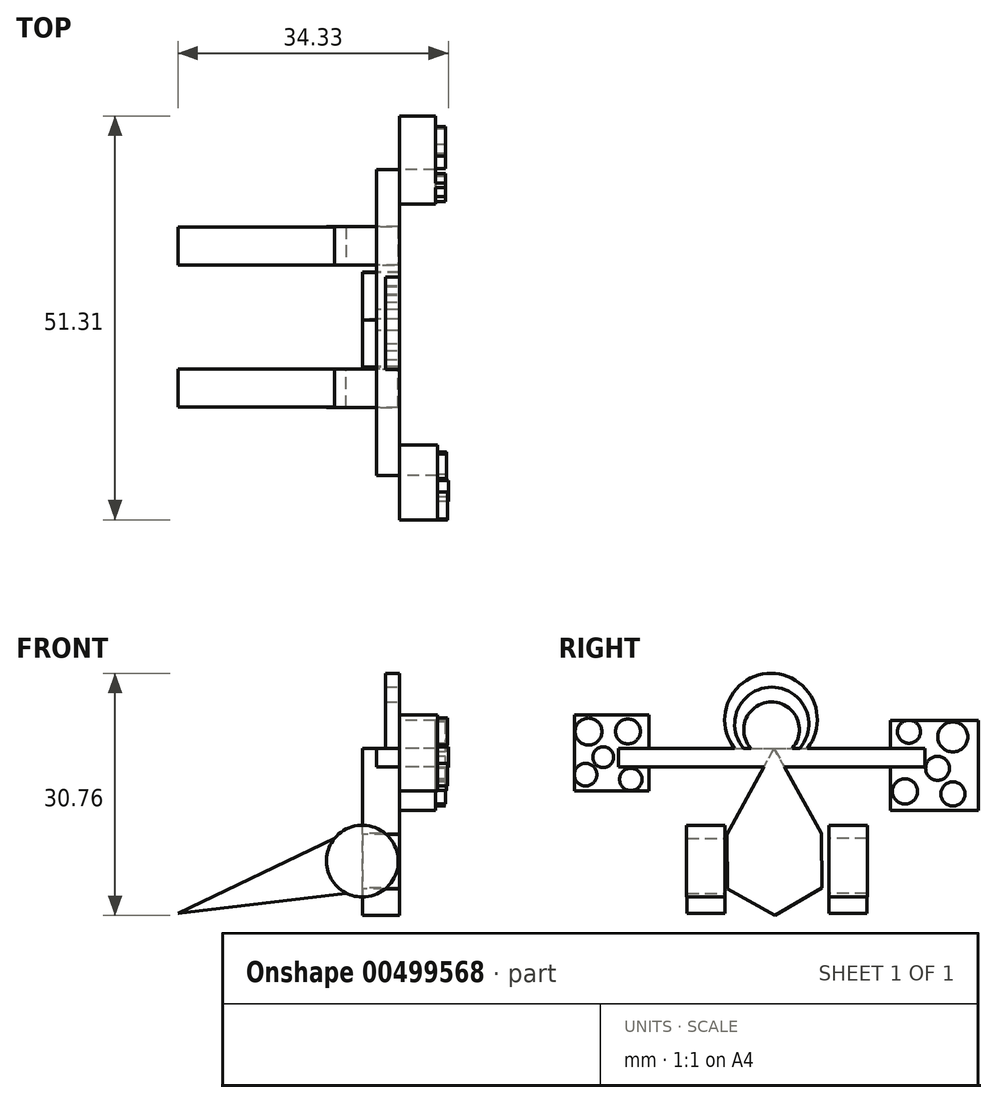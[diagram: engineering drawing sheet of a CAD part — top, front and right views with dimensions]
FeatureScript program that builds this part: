
annotation { "Feature Type Name" : "Feature", "Feature Type Description" : "" }
export const myFeature = defineFeature(function(context is Context, id is Id, definition is map)
    precondition{}
    {
        {
            var Q0;
            Q0=qCreatedBy(makeId("Front.planeOp"),FACE);
            var sketch = newSketch(context, id + "F0", { "sketchPlane" : qUnion([Q0])});
            skCircle(sketch, "E0", {"center": v(0, 0) * mm, "radius": 91.11 * mm});
            skSolve(sketch);
        }
        {
            var Q0;
            Q0=makeQuery(id+"F0.imprint","IMPRINT",FACE,{"disambiguationData":[TD([[makeQuery(id+"F0.imprint","IMPRINT",EDGE,{"derivedFrom":sQuery(id+"F0.wireOp",EDGE,"E0")}),1.0]])]});
            extrude(context, id + "F1", {"entities" : qUnion([Q0]), "depth" : 98.04 * mm});
        }
        {
            var Q0;
            Q0=makeQuery(id+"F1.opExtrude","CAP_FACE",FACE,{"disambiguationData":[OSD([sQuery(id+"F0.wireOp",EDGE,"E0")])],"isStart":true});
            var sketch = newSketch(context, id + "F2", { "sketchPlane" : qUnion([Q0])});
            skLineSegment(sketch, "E1", {"start": v(0, 91.11) * mm, "end": v(-434.23, -92.92) * mm});
            skLineSegment(sketch, "E2", {"start": v(0, -76.65) * mm, "end": v(-434.23, -92.92) * mm});
            skLineSegment(sketch, "E3", {"start": v(0, 91.11) * mm, "end": v(468.1, -132.24) * mm});
            skLineSegment(sketch, "E4", {"start": v(468.1, -132.24) * mm, "end": v(0, -76.65) * mm});
            skSolve(sketch);
        }
        {
            var Q0;
            {var subQ0=sQuery(id+"F2.wireOp",EDGE,"E4");var subQ1=sQuery(id+"F2.wireOp",EDGE,"E3");var subQ2=makeQuery(id+"F2.imprint","INTERSECT",VERTEX,{"derivedFrom":[subQ1,subQ0]});Q0=makeQuery(id+"F2.imprint","IMPRINT",FACE,{"disambiguationData":[TD([[makeQuery(id+"F2.imprint","IMPRINT",EDGE,{"disambiguationData":[TD([[subQ2,1.0]])],"derivedFrom":subQ1}),-1.0]])]});}
            extrude(context, id + "F3", {"entities" : qUnion([Q0]), "operationType" : NewBodyOperationType.ADD, "oppositeDirection" : true, "depth" : 96.52 * mm});
        }
        {
            var Q0;
            Q0=makeQuery(id+"F1.opExtrude","SWEPT_BODY",BODY,{"disambiguationData":[OSD([sQuery(id+"F0.wireOp",EDGE,"E0")])]});
            var Q1;
            Q1=qCreatedBy(makeId("Front.planeOp"),FACE);
            mirror(context, id + "F4", {"entities" : qUnion([Q0]), "mirrorPlane" : qUnion([Q1])});
        }
        {
            var Q0;
            Q0=makeQuery(id+"F4.opPattern","COPY",BODY,{"derivedFrom":makeQuery(id+"F1.opExtrude","SWEPT_BODY",BODY,{"disambiguationData":[OSD([sQuery(id+"F0.wireOp",EDGE,"E0")])]}),"instanceName":"1"});
            transform(context, id + "F5", {"entities" : qUnion([Q0]), "transformType" : TransformType.TRANSLATION_3D, "dx" : 0 * mm, "dy" : 264.16 * mm, "dz" : 0 * mm, "makeCopy" : false});
        }
        {
            var Q0;
            Q0=qCreatedBy(makeId("Right.planeOp"),FACE);
            var sketch = newSketch(context, id + "F6", { "sketchPlane" : qUnion([Q0])});
            skCircle(sketch, "E5.cCircle", {"center": v(125.72, 0) * mm, "radius": 119.75 * mm, "construction": true});
            skLineSegment(sketch, "E5.0", {"start": v(5.37, 68.07) * mm, "end": v(124.5, 138.26) * mm});
            skLineSegment(sketch, "E5.1", {"start": v(124.5, 138.26) * mm, "end": v(244.85, 70.2) * mm});
            skLineSegment(sketch, "E5.2", {"start": v(244.85, 70.2) * mm, "end": v(246.08, -68.07) * mm});
            skLineSegment(sketch, "E5.3", {"start": v(246.08, -68.07) * mm, "end": v(126.95, -138.26) * mm});
            skLineSegment(sketch, "E5.4", {"start": v(126.95, -138.26) * mm, "end": v(6.6, -70.2) * mm});
            skLineSegment(sketch, "E5.5", {"start": v(6.6, -70.2) * mm, "end": v(5.37, 68.07) * mm});
            skPoint(sketch, "E5.0.midPoint", {"position": v(64.93, 103.17) * mm});
            skSolve(sketch);
        }
        {
            var Q0;
            Q0=makeQuery(id+"F6.imprint","IMPRINT",FACE,{"disambiguationData":[TD([[makeQuery(id+"F6.imprint","IMPRINT",EDGE,{"derivedFrom":sQuery(id+"F6.wireOp",EDGE,"E5.0")}),-1.0]])]});
            extrude(context, id + "F7", {"entities" : qUnion([Q0]), "depth" : 93.98 * mm});
        }
        {
            var Q0;
            Q0=makeQuery(id+"F7.opExtrude","CAP_FACE",FACE,{"disambiguationData":[OSD([sQuery(id+"F6.wireOp",EDGE,"E5.0"),sQuery(id+"F6.wireOp",EDGE,"E5.1"),sQuery(id+"F6.wireOp",EDGE,"E5.2"),sQuery(id+"F6.wireOp",EDGE,"E5.3"),sQuery(id+"F6.wireOp",EDGE,"E5.4"),sQuery(id+"F6.wireOp",EDGE,"E5.5")])],"isStart":false});
            var sketch = newSketch(context, id + "F8", { "sketchPlane" : qUnion([Q0])});
            skLineSegment(sketch, "E6", {"start": v(5.37, 68.07) * mm, "end": v(124.5, 286.89) * mm});
            skLineSegment(sketch, "E7", {"start": v(244.85, 70.2) * mm, "end": v(124.5, 286.89) * mm});
            skSolve(sketch);
        }
        {
            var Q0;
            Q0=makeQuery(id+"F8.imprint","IMPRINT",FACE,{"disambiguationData":[TD([[makeQuery(id+"F8.imprint","IMPRINT",EDGE,{"derivedFrom":sQuery(id+"F8.wireOp",EDGE,"E6")}),-1.0]])]});
            extrude(context, id + "F9", {"entities" : qUnion([Q0]), "operationType" : NewBodyOperationType.ADD, "oppositeDirection" : true, "depth" : 93.98 * mm});
        }
        {
            var Q0;
            {var subQ0=sQuery(id+"F6.wireOp",EDGE,"E5.1");var subQ1=sQuery(id+"F6.wireOp",EDGE,"E5.0");Q0=makeQuery(id+"F9.boolean.opBoolean","MERGE",FACE,{"derivedFrom":[makeQuery(id+"F7.opExtrude","CAP_FACE",FACE,{"disambiguationData":[OSD([subQ1,subQ0,sQuery(id+"F6.wireOp",EDGE,"E5.2"),sQuery(id+"F6.wireOp",EDGE,"E5.3"),sQuery(id+"F6.wireOp",EDGE,"E5.4"),sQuery(id+"F6.wireOp",EDGE,"E5.5")])],"isStart":false}),makeQuery(id+"F9.opExtrude","CAP_FACE",FACE,{"disambiguationData":[OSD([subQ1,subQ0,sQuery(id+"F8.wireOp",EDGE,"E6"),sQuery(id+"F8.wireOp",EDGE,"E7")])],"isStart":true})]});}
            var sketch = newSketch(context, id + "F10", { "sketchPlane" : qUnion([Q0])});
            skLineSegment(sketch, "E8.bottom", {"start": v(-270.15, 286.89) * mm, "end": v(507.6, 286.89) * mm});
            skLineSegment(sketch, "E8.top", {"start": v(-270.15, 238.84) * mm, "end": v(507.6, 238.84) * mm});
            skLineSegment(sketch, "E8.left", {"start": v(-270.15, 286.89) * mm, "end": v(-270.15, 238.84) * mm});
            skLineSegment(sketch, "E8.right", {"start": v(507.6, 286.89) * mm, "end": v(507.6, 238.84) * mm});
            skSolve(sketch);
        }
        {
            var Q0;
            Q0=qSketchRegion(id+"F10",true);
            extrude(context, id + "F11", {"entities" : qUnion([Q0]), "operationType" : NewBodyOperationType.ADD, "oppositeDirection" : true, "depth" : 58.42 * mm});
        }
        {
            var Q0;
            {var subQ0=sQuery(id+"F6.wireOp",EDGE,"E5.1");var subQ1=sQuery(id+"F6.wireOp",EDGE,"E5.0");Q0=makeQuery(id+"F11.boolean.opBoolean","MERGE",FACE,{"derivedFrom":[makeQuery(id+"F9.boolean.opBoolean","MERGE",FACE,{"derivedFrom":[makeQuery(id+"F7.opExtrude","CAP_FACE",FACE,{"disambiguationData":[OSD([subQ1,subQ0,sQuery(id+"F6.wireOp",EDGE,"E5.2"),sQuery(id+"F6.wireOp",EDGE,"E5.3"),sQuery(id+"F6.wireOp",EDGE,"E5.4"),sQuery(id+"F6.wireOp",EDGE,"E5.5")])],"isStart":false}),makeQuery(id+"F9.opExtrude","CAP_FACE",FACE,{"disambiguationData":[OSD([subQ1,subQ0,sQuery(id+"F8.wireOp",EDGE,"E6"),sQuery(id+"F8.wireOp",EDGE,"E7")])],"isStart":true})]}),makeQuery(id+"F11.opExtrude","CAP_FACE",FACE,{"disambiguationData":[OSD([sQuery(id+"F10.wireOp",EDGE,"E8.bottom"),sQuery(id+"F10.wireOp",EDGE,"E8.top"),sQuery(id+"F10.wireOp",EDGE,"E8.left"),sQuery(id+"F10.wireOp",EDGE,"E8.right")])],"isStart":true})]});}
            var sketch = newSketch(context, id + "F12", { "sketchPlane" : qUnion([Q0])});
            skLineSegment(sketch, "E9.bottom", {"start": v(-383, 179.03) * mm, "end": v(-193.33, 179.03) * mm});
            skLineSegment(sketch, "E9.top", {"start": v(-383, 371.33) * mm, "end": v(-193.33, 371.33) * mm});
            skLineSegment(sketch, "E9.left", {"start": v(-383, 179.03) * mm, "end": v(-383, 371.33) * mm});
            skLineSegment(sketch, "E9.right", {"start": v(-193.33, 179.03) * mm, "end": v(-193.33, 371.33) * mm});
            skSolve(sketch);
        }
        {
            var Q0;
            {var subQ1=sQuery(id+"F12.wireOp",EDGE,"E9.bottom");Q0=makeQuery(id+"F12.imprint","IMPRINT",FACE,{"disambiguationData":[TD([[makeQuery(id+"F12.imprint","IMPRINT",EDGE,{"derivedFrom":subQ1}),1.0]])]});}
            extrude(context, id + "F13", {"entities" : qUnion([Q0]), "depth" : 96.52 * mm});
        }
        {
            var Q0;
            {var subQ0=sQuery(id+"F6.wireOp",EDGE,"E5.1");var subQ1=sQuery(id+"F6.wireOp",EDGE,"E5.0");Q0=makeQuery(id+"F11.boolean.opBoolean","MERGE",FACE,{"derivedFrom":[makeQuery(id+"F9.boolean.opBoolean","MERGE",FACE,{"derivedFrom":[makeQuery(id+"F7.opExtrude","CAP_FACE",FACE,{"disambiguationData":[OSD([subQ1,subQ0,sQuery(id+"F6.wireOp",EDGE,"E5.2"),sQuery(id+"F6.wireOp",EDGE,"E5.3"),sQuery(id+"F6.wireOp",EDGE,"E5.4"),sQuery(id+"F6.wireOp",EDGE,"E5.5")])],"isStart":false}),makeQuery(id+"F9.opExtrude","CAP_FACE",FACE,{"disambiguationData":[OSD([subQ1,subQ0,sQuery(id+"F8.wireOp",EDGE,"E6"),sQuery(id+"F8.wireOp",EDGE,"E7")])],"isStart":true})]}),makeQuery(id+"F11.opExtrude","CAP_FACE",FACE,{"disambiguationData":[OSD([sQuery(id+"F10.wireOp",EDGE,"E8.bottom"),sQuery(id+"F10.wireOp",EDGE,"E8.top"),sQuery(id+"F10.wireOp",EDGE,"E8.left"),sQuery(id+"F10.wireOp",EDGE,"E8.right")])],"isStart":true})]});}
            var sketch = newSketch(context, id + "F14", { "sketchPlane" : qUnion([Q0])});
            skLineSegment(sketch, "E10.bottom", {"start": v(643.3, 129.12) * mm, "end": v(420.02, 129.12) * mm});
            skLineSegment(sketch, "E10.top", {"start": v(643.3, 357.33) * mm, "end": v(420.02, 357.33) * mm});
            skLineSegment(sketch, "E10.left", {"start": v(643.3, 129.12) * mm, "end": v(643.3, 357.33) * mm});
            skLineSegment(sketch, "E10.right", {"start": v(420.02, 129.12) * mm, "end": v(420.02, 357.33) * mm});
            skSolve(sketch);
        }
        {
            var Q0;
            {var subQ1=sQuery(id+"F14.wireOp",EDGE,"E10.bottom");Q0=makeQuery(id+"F14.imprint","IMPRINT",FACE,{"disambiguationData":[TD([[makeQuery(id+"F14.imprint","IMPRINT",EDGE,{"derivedFrom":subQ1}),-1.0]])]});}
            extrude(context, id + "F15", {"entities" : qUnion([Q0]), "depth" : 91.44 * mm});
        }
        {
            var Q0;
            Q0=makeQuery(id+"F13.opExtrude","CAP_FACE",FACE,{"disambiguationData":[OSD([sQuery(id+"F10.wireOp",EDGE,"E8.bottom"),sQuery(id+"F10.wireOp",EDGE,"E8.top"),sQuery(id+"F10.wireOp",EDGE,"E8.left"),sQuery(id+"F12.wireOp",EDGE,"E9.bottom"),sQuery(id+"F12.wireOp",EDGE,"E9.top"),sQuery(id+"F12.wireOp",EDGE,"E9.left"),sQuery(id+"F12.wireOp",EDGE,"E9.right")])],"isStart":false});
            var sketch = newSketch(context, id + "F16", { "sketchPlane" : qUnion([Q0])});
            skCircle(sketch, "E11", {"center": v(-239.34, 329.1) * mm, "radius": 32.95 * mm});
            skPoint(sketch, "E11.centerSnap0", {"position": v(-193.33, 329.1) * mm});
            skCircle(sketch, "E12", {"center": v(-346.66, 329.1) * mm, "radius": 34.15 * mm});
            skCircle(sketch, "E13", {"center": v(-354.15, 219.75) * mm, "radius": 28.7 * mm});
            skCircle(sketch, "E14", {"center": v(-239.34, 207.67) * mm, "radius": 28.52 * mm});
            skCircle(sketch, "E15", {"center": v(-309.5, 263.98) * mm, "radius": 26.29 * mm});
            skSolve(sketch);
        }
        {
            var Q0;
            Q0=makeQuery(id+"F16.imprint","IMPRINT",FACE,{"disambiguationData":[TD([[makeQuery(id+"F16.imprint","IMPRINT",EDGE,{"derivedFrom":sQuery(id+"F16.wireOp",EDGE,"E12")}),1.0]])]});
            var Q1;
            Q1=sQuery(id+"F16.wireOp",EDGE,"E12");
            extrude(context, id + "F17", {"entities" : qUnion([Q0]), "operationType" : NewBodyOperationType.ADD, "surfaceEntities" : qUnion([Q1]), "depth" : 25.4 * mm});
        }
        {
            var Q0;
            Q0=makeQuery(id+"F13.opExtrude","CAP_FACE",FACE,{"disambiguationData":[OSD([sQuery(id+"F10.wireOp",EDGE,"E8.bottom"),sQuery(id+"F10.wireOp",EDGE,"E8.top"),sQuery(id+"F10.wireOp",EDGE,"E8.left"),sQuery(id+"F12.wireOp",EDGE,"E9.bottom"),sQuery(id+"F12.wireOp",EDGE,"E9.top"),sQuery(id+"F12.wireOp",EDGE,"E9.left"),sQuery(id+"F12.wireOp",EDGE,"E9.right")])],"isStart":false});
            var sketch = newSketch(context, id + "F18", { "sketchPlane" : qUnion([Q0])});
            skCircle(sketch, "E16", {"center": v(-246.53, 329.52) * mm, "radius": 31.43 * mm});
            skSolve(sketch);
        }
        {
            var Q0;
            Q0=makeQuery(id+"F18.imprint","IMPRINT",FACE,{"disambiguationData":[TD([[makeQuery(id+"F18.imprint","IMPRINT",EDGE,{"derivedFrom":sQuery(id+"F18.wireOp",EDGE,"E16")}),1.0]])]});
            var Q1;
            Q1=sQuery(id+"F18.wireOp",EDGE,"E16");
            extrude(context, id + "F19", {"entities" : qUnion([Q0]), "operationType" : NewBodyOperationType.ADD, "surfaceEntities" : qUnion([Q1]), "endBound" : BoundingType.SYMMETRIC, "depth" : 45.72 * mm});
        }
        {
            var Q0;
            Q0=makeQuery(id+"F16.imprint","IMPRINT",FACE,{"disambiguationData":[TD([[makeQuery(id+"F16.imprint","IMPRINT",EDGE,{"derivedFrom":sQuery(id+"F16.wireOp",EDGE,"E15")}),1.0]])]});
            var Q1;
            Q1=sQuery(id+"F16.wireOp",EDGE,"E15");
            extrude(context, id + "F20", {"entities" : qUnion([Q0]), "operationType" : NewBodyOperationType.ADD, "surfaceEntities" : qUnion([Q1]), "depth" : 27.94 * mm});
        }
        {
            var Q0;
            Q0=makeQuery(id+"F16.imprint","IMPRINT",FACE,{"disambiguationData":[TD([[makeQuery(id+"F16.imprint","IMPRINT",EDGE,{"derivedFrom":sQuery(id+"F16.wireOp",EDGE,"E13")}),1.0]])]});
            var Q1;
            Q1=sQuery(id+"F16.wireOp",EDGE,"E13");
            extrude(context, id + "F21", {"entities" : qUnion([Q0]), "operationType" : NewBodyOperationType.ADD, "surfaceEntities" : qUnion([Q1]), "depth" : 25.4 * mm});
        }
        {
            var Q0;
            Q0=makeQuery(id+"F16.imprint","IMPRINT",FACE,{"disambiguationData":[TD([[makeQuery(id+"F16.imprint","IMPRINT",EDGE,{"derivedFrom":sQuery(id+"F16.wireOp",EDGE,"E14")}),1.0]])]});
            var Q1;
            Q1=sQuery(id+"F16.wireOp",EDGE,"E14");
            extrude(context, id + "F22", {"entities" : qUnion([Q0]), "operationType" : NewBodyOperationType.ADD, "surfaceEntities" : qUnion([Q1]), "depth" : 22.86 * mm});
        }
        {
            var Q0;
            Q0=makeQuery(id+"F15.opExtrude","CAP_FACE",FACE,{"disambiguationData":[OSD([sQuery(id+"F10.wireOp",EDGE,"E8.bottom"),sQuery(id+"F10.wireOp",EDGE,"E8.top"),sQuery(id+"F10.wireOp",EDGE,"E8.right"),sQuery(id+"F14.wireOp",EDGE,"E10.bottom"),sQuery(id+"F14.wireOp",EDGE,"E10.top"),sQuery(id+"F14.wireOp",EDGE,"E10.left"),sQuery(id+"F14.wireOp",EDGE,"E10.right")])],"isStart":false});
            var sketch = newSketch(context, id + "F23", { "sketchPlane" : qUnion([Q0])});
            skCircle(sketch, "E17", {"center": v(578.72, 315.62) * mm, "radius": 38.04 * mm});
            skCircle(sketch, "E18", {"center": v(457.24, 177.07) * mm, "radius": 32 * mm});
            skCircle(sketch, "E19", {"center": v(579.03, 170.7) * mm, "radius": 30.77 * mm});
            skCircle(sketch, "E20", {"center": v(467.35, 328.58) * mm, "radius": 29.36 * mm});
            skCircle(sketch, "E21", {"center": v(540.02, 235.78) * mm, "radius": 30.37 * mm});
            skSolve(sketch);
        }
        {
            var Q0;
            {var subQ0=sQuery(id+"F23.wireOp",EDGE,"E20");var subQ1=makeQuery(id+"F15.opExtrude","CAP_EDGE",EDGE,{"disambiguationData":[OSD([sQuery(id+"F14.wireOp",EDGE,"E10.top")])],"isStart":false});var subQ2=makeQuery(id+"F23.imprint","INTERSECT",VERTEX,{"disambiguationData":[OD(0.0)],"derivedFrom":[subQ1,subQ0]});Q0=makeQuery(id+"F23.imprint","IMPRINT",FACE,{"disambiguationData":[TD([[makeQuery(id+"F23.imprint","IMPRINT",EDGE,{"disambiguationData":[TD([[subQ2,1.0]])],"derivedFrom":subQ0}),1.0]])]});}
            var Q1;
            Q1=sQuery(id+"F23.wireOp",EDGE,"E20");
            extrude(context, id + "F24", {"entities" : qUnion([Q0]), "operationType" : NewBodyOperationType.ADD, "surfaceEntities" : qUnion([Q1]), "depth" : 25.4 * mm});
        }
        {
            var Q0;
            Q0=makeQuery(id+"F23.imprint","IMPRINT",FACE,{"disambiguationData":[TD([[makeQuery(id+"F23.imprint","IMPRINT",EDGE,{"derivedFrom":sQuery(id+"F23.wireOp",EDGE,"E17")}),1.0]])]});
            var Q1;
            Q1=sQuery(id+"F23.wireOp",EDGE,"E17");
            extrude(context, id + "F25", {"entities" : qUnion([Q0]), "operationType" : NewBodyOperationType.ADD, "surfaceEntities" : qUnion([Q1]), "depth" : 25.4 * mm});
        }
        {
            var Q0;
            Q0=makeQuery(id+"F23.imprint","IMPRINT",FACE,{"disambiguationData":[TD([[makeQuery(id+"F23.imprint","IMPRINT",EDGE,{"derivedFrom":sQuery(id+"F23.wireOp",EDGE,"E21")}),1.0]])]});
            var Q1;
            Q1=sQuery(id+"F23.wireOp",EDGE,"E21");
            extrude(context, id + "F26", {"entities" : qUnion([Q0]), "operationType" : NewBodyOperationType.ADD, "surfaceEntities" : qUnion([Q1]), "depth" : 25.4 * mm});
        }
        {
            var Q0;
            Q0=makeQuery(id+"F23.imprint","IMPRINT",FACE,{"disambiguationData":[TD([[makeQuery(id+"F23.imprint","IMPRINT",EDGE,{"derivedFrom":sQuery(id+"F23.wireOp",EDGE,"E18")}),1.0]])]});
            var Q1;
            Q1=sQuery(id+"F23.wireOp",EDGE,"E18");
            extrude(context, id + "F27", {"entities" : qUnion([Q0]), "operationType" : NewBodyOperationType.ADD, "surfaceEntities" : qUnion([Q1]), "depth" : 25.4 * mm});
        }
        {
            var Q0;
            Q0=makeQuery(id+"F23.imprint","IMPRINT",FACE,{"disambiguationData":[TD([[makeQuery(id+"F23.imprint","IMPRINT",EDGE,{"derivedFrom":sQuery(id+"F23.wireOp",EDGE,"E19")}),1.0]])]});
            extrude(context, id + "F28", {"entities" : qUnion([Q0]), "operationType" : NewBodyOperationType.ADD, "depth" : 25.4 * mm});
        }
        {
            var Q0;
            {var subQ0=sQuery(id+"F6.wireOp",EDGE,"E5.1");var subQ1=sQuery(id+"F6.wireOp",EDGE,"E5.0");Q0=makeQuery(id+"F11.boolean.opBoolean","MERGE",FACE,{"derivedFrom":[makeQuery(id+"F9.boolean.opBoolean","MERGE",FACE,{"derivedFrom":[makeQuery(id+"F7.opExtrude","CAP_FACE",FACE,{"disambiguationData":[OSD([subQ1,subQ0,sQuery(id+"F6.wireOp",EDGE,"E5.2"),sQuery(id+"F6.wireOp",EDGE,"E5.3"),sQuery(id+"F6.wireOp",EDGE,"E5.4"),sQuery(id+"F6.wireOp",EDGE,"E5.5")])],"isStart":false}),makeQuery(id+"F9.opExtrude","CAP_FACE",FACE,{"disambiguationData":[OSD([subQ1,subQ0,sQuery(id+"F8.wireOp",EDGE,"E6"),sQuery(id+"F8.wireOp",EDGE,"E7")])],"isStart":true})]}),makeQuery(id+"F11.opExtrude","CAP_FACE",FACE,{"disambiguationData":[OSD([sQuery(id+"F10.wireOp",EDGE,"E8.bottom"),sQuery(id+"F10.wireOp",EDGE,"E8.top"),sQuery(id+"F10.wireOp",EDGE,"E8.left"),sQuery(id+"F10.wireOp",EDGE,"E8.right")])],"isStart":true})]});}
            var sketch = newSketch(context, id + "F29", { "sketchPlane" : qUnion([Q0])});
            skArc(sketch, "E22", {"start": v(233.56, 286.89) * mm, "mid": v(116.78, 510.28) * mm, "end": v(0, 286.89) * mm});
            skSolve(sketch);
        }
        {
            var Q0;
            Q0=sQuery(id+"F29.wireOp",EDGE,"E22");
            extrude(context, id + "F30", {"bodyType" : ToolBodyType.SURFACE, "surfaceEntities" : qUnion([Q0]), "oppositeDirection" : true, "depth" : 55.88 * mm});
        }
        {
            var Q0;
            {var subQ0=sQuery(id+"F6.wireOp",EDGE,"E5.1");var subQ1=sQuery(id+"F6.wireOp",EDGE,"E5.0");Q0=makeQuery(id+"F11.boolean.opBoolean","MERGE",FACE,{"derivedFrom":[makeQuery(id+"F9.boolean.opBoolean","MERGE",FACE,{"derivedFrom":[makeQuery(id+"F7.opExtrude","CAP_FACE",FACE,{"disambiguationData":[OSD([subQ1,subQ0,sQuery(id+"F6.wireOp",EDGE,"E5.2"),sQuery(id+"F6.wireOp",EDGE,"E5.3"),sQuery(id+"F6.wireOp",EDGE,"E5.4"),sQuery(id+"F6.wireOp",EDGE,"E5.5")])],"isStart":false}),makeQuery(id+"F9.opExtrude","CAP_FACE",FACE,{"disambiguationData":[OSD([subQ1,subQ0,sQuery(id+"F8.wireOp",EDGE,"E6"),sQuery(id+"F8.wireOp",EDGE,"E7")])],"isStart":true})]}),makeQuery(id+"F11.opExtrude","CAP_FACE",FACE,{"disambiguationData":[OSD([sQuery(id+"F10.wireOp",EDGE,"E8.bottom"),sQuery(id+"F10.wireOp",EDGE,"E8.top"),sQuery(id+"F10.wireOp",EDGE,"E8.left"),sQuery(id+"F10.wireOp",EDGE,"E8.right")])],"isStart":true})]});}
            var sketch = newSketch(context, id + "F31", { "sketchPlane" : qUnion([Q0])});
            skArc(sketch, "E23", {"start": v(209.6, 286.89) * mm, "mid": v(116.89, 477.07) * mm, "end": v(24.18, 286.89) * mm});
            skArc(sketch, "E24", {"start": v(190.35, 286.89) * mm, "mid": v(118.69, 441.99) * mm, "end": v(47.02, 286.89) * mm});
            skArc(sketch, "E25", {"start": v(170.94, 286.89) * mm, "mid": v(118.21, 404.41) * mm, "end": v(65.48, 286.89) * mm});
            skArc(sketch, "E26", {"start": v(147.33, 286.89) * mm, "mid": v(117.05, 359.38) * mm, "end": v(86.77, 286.89) * mm});
            skSolve(sketch);
        }
        {
            var Q0;
            {var subQ0=sQuery(id+"F31.wireOp",EDGE,"E23");Q0=makeQuery(id+"F31.imprint","IMPRINT",FACE,{"disambiguationData":[TD([[makeQuery(id+"F31.imprint","IMPRINT",EDGE,{"derivedFrom":subQ0}),1.0]])]});}
            var Q1;
            {var subQ0=sQuery(id+"F31.wireOp",EDGE,"E26");Q1=makeQuery(id+"F31.imprint","IMPRINT",FACE,{"disambiguationData":[TD([[makeQuery(id+"F31.imprint","IMPRINT",EDGE,{"derivedFrom":subQ0}),1.0]])]});}
            var Q2;
            {var subQ0=sQuery(id+"F31.wireOp",EDGE,"E25");Q2=makeQuery(id+"F31.imprint","IMPRINT",FACE,{"disambiguationData":[TD([[makeQuery(id+"F31.imprint","IMPRINT",EDGE,{"derivedFrom":subQ0}),1.0]])]});}
            extrude(context, id + "F32", {"entities" : qUnion([Q0, Q1, Q2]), "operationType" : NewBodyOperationType.ADD, "oppositeDirection" : true, "depth" : 35.56 * mm});
        }
        {
            var Q0;
            Q0=makeQuery(id+"F7.opExtrude","SWEPT_BODY",BODY,{"disambiguationData":[OSD([sQuery(id+"F6.wireOp",EDGE,"E5.0"),sQuery(id+"F6.wireOp",EDGE,"E5.1"),sQuery(id+"F6.wireOp",EDGE,"E5.2"),sQuery(id+"F6.wireOp",EDGE,"E5.3"),sQuery(id+"F6.wireOp",EDGE,"E5.4"),sQuery(id+"F6.wireOp",EDGE,"E5.5")])]});
            var Q1;
            Q1=makeQuery(id+"F13.opExtrude","SWEPT_BODY",BODY,{"disambiguationData":[OSD([sQuery(id+"F10.wireOp",EDGE,"E8.bottom"),sQuery(id+"F10.wireOp",EDGE,"E8.top"),sQuery(id+"F10.wireOp",EDGE,"E8.left"),sQuery(id+"F12.wireOp",EDGE,"E9.bottom"),sQuery(id+"F12.wireOp",EDGE,"E9.top"),sQuery(id+"F12.wireOp",EDGE,"E9.left"),sQuery(id+"F12.wireOp",EDGE,"E9.right")])]});
            var Q2;
            Q2=makeQuery(id+"F15.opExtrude","SWEPT_BODY",BODY,{"disambiguationData":[OSD([sQuery(id+"F10.wireOp",EDGE,"E8.bottom"),sQuery(id+"F10.wireOp",EDGE,"E8.top"),sQuery(id+"F10.wireOp",EDGE,"E8.right"),sQuery(id+"F14.wireOp",EDGE,"E10.bottom"),sQuery(id+"F14.wireOp",EDGE,"E10.top"),sQuery(id+"F14.wireOp",EDGE,"E10.left"),sQuery(id+"F14.wireOp",EDGE,"E10.right")])]});
            var Q3;
            Q3=makeQuery(id+"F30.opExtrude","SWEPT_BODY",BODY,{"disambiguationData":[OSD([sQuery(id+"F29.wireOp",EDGE,"E22")])]});
            var Q4;
            Q4=makeQuery(id+"F4.opPattern","COPY",BODY,{"derivedFrom":makeQuery(id+"F1.opExtrude","SWEPT_BODY",BODY,{"disambiguationData":[OSD([sQuery(id+"F0.wireOp",EDGE,"E0")])]}),"instanceName":"1"});
            var Q5;
            Q5=makeQuery(id+"F1.opExtrude","SWEPT_BODY",BODY,{"disambiguationData":[OSD([sQuery(id+"F0.wireOp",EDGE,"E0")])]});
            var Q6;
            Q6=qCreatedBy(makeId("Origin.pointOp"),VERTEX);
            transform(context, id + "F33", {"entities" : qUnion([Q0, Q1, Q2, Q3, Q4, Q5]), "transformType" : TransformType.SCALE_UNIFORMLY, "scale" : 2 / 40, "scalePoint" : qUnion([Q6]), "makeCopy" : false});
        }
    });
